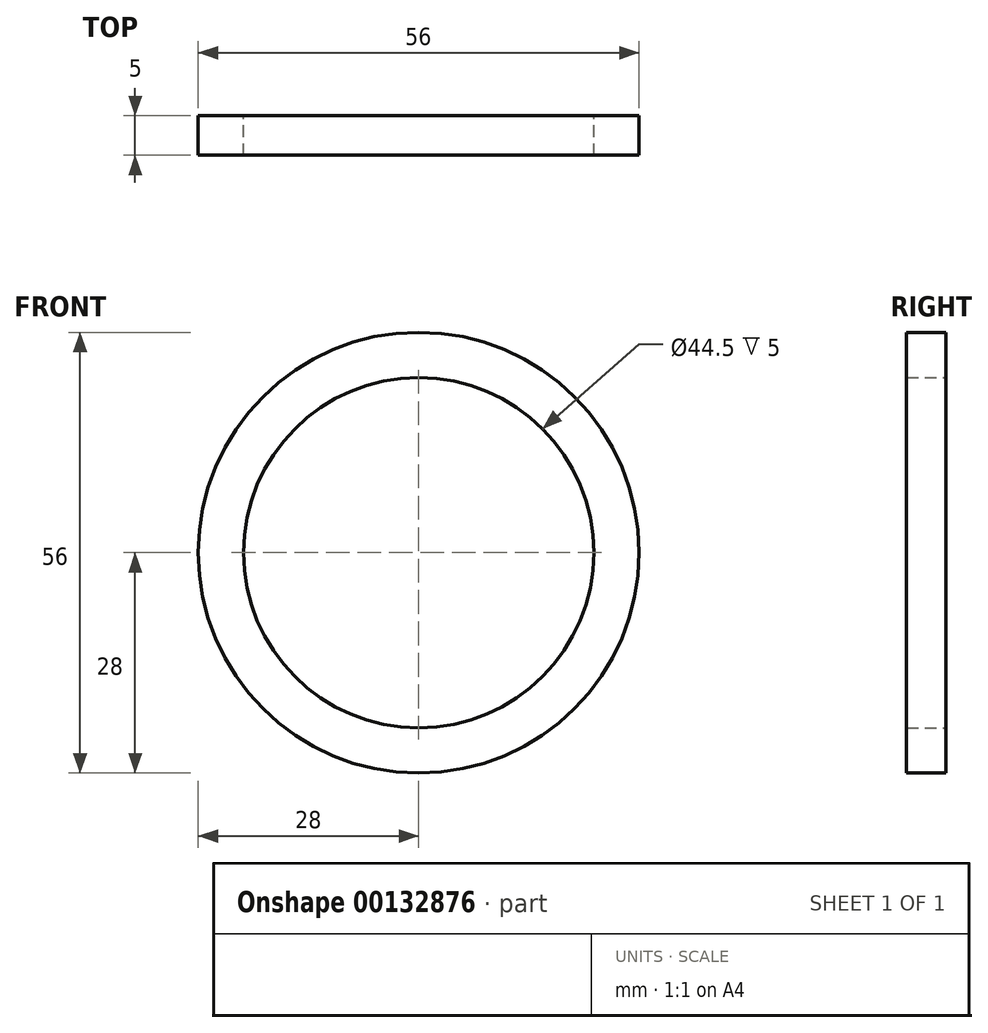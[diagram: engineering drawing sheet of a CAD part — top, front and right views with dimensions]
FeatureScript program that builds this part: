
annotation { "Feature Type Name" : "Feature", "Feature Type Description" : "" }
export const myFeature = defineFeature(function(context is Context, id is Id, definition is map)
    precondition{}
    {
        {
            var Q0;
            Q0=qCreatedBy(makeId("Front.planeOp"),FACE);
            var sketch = newSketch(context, id + "F0", { "sketchPlane" : qUnion([Q0])});
            skCircle(sketch, "E0", {"center": v(0, 0) * mm, "radius": 28 * mm});
            skCircle(sketch, "E1", {"center": v(0, 0) * mm, "radius": 22.25 * mm});
            skSolve(sketch);
        }
        {
            var Q0;
            Q0 = qSketchRegion(id + "F0", true);
            extrude(context, id + "F1", {"entities" : qUnion([Q0]), "depth" : 5 * mm});
        }
    });
